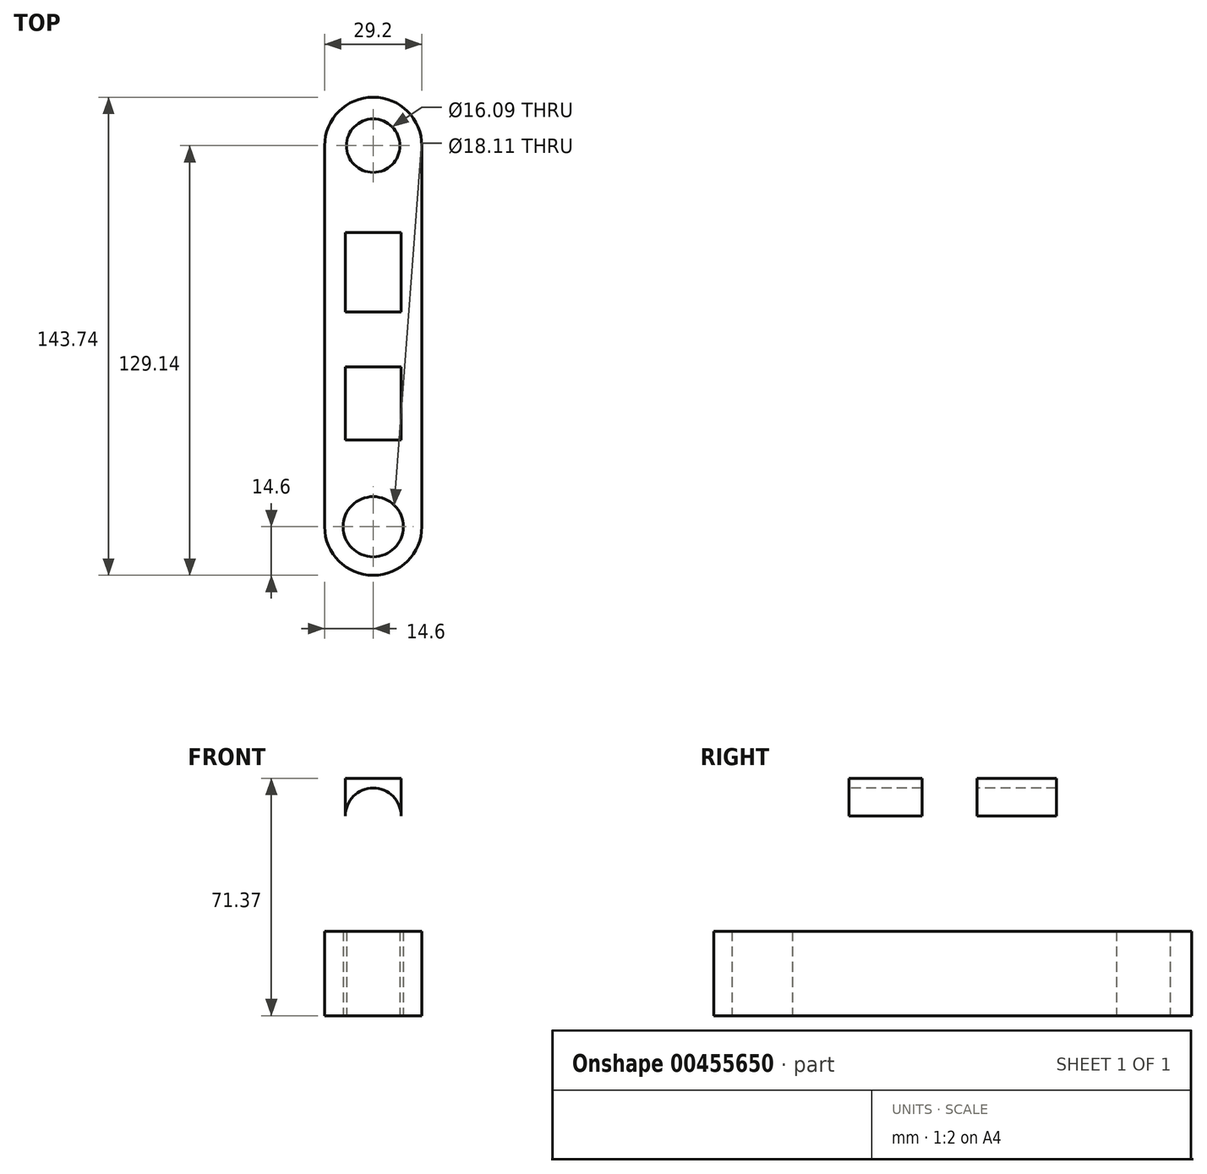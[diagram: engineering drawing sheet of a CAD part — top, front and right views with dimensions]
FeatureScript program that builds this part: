
annotation { "Feature Type Name" : "Feature", "Feature Type Description" : "" }
export const myFeature = defineFeature(function(context is Context, id is Id, definition is map)
    precondition{}
    {
        {
            var Q0;
            Q0=qCreatedBy(makeId("Top.planeOp"),FACE);
            var sketch = newSketch(context, id + "F0", { "sketchPlane" : qUnion([Q0])});
            skLineSegment(sketch, "E0.left", {"start": v(14.6, 57.27) * mm, "end": v(14.6, -57.27) * mm});
            skLineSegment(sketch, "E0.right", {"start": v(-14.6, 57.27) * mm, "end": v(-14.6, -57.27) * mm});
            skPoint(sketch, "E0.middle", {"position": v(0, 0) * mm});
            skArc(sketch, "E1", {"start": v(14.6, 57.27) * mm, "mid": v(0, 71.87) * mm, "end": v(-14.6, 57.27) * mm});
            skArc(sketch, "E2", {"start": v(14.6, -57.27) * mm, "mid": v(0, -71.87) * mm, "end": v(-14.6, -57.27) * mm});
            skCircle(sketch, "E3", {"center": v(0, 57.27) * mm, "radius": 8.04 * mm});
            skCircle(sketch, "E4", {"center": v(0, -57.27) * mm, "radius": 9.05 * mm});
            skSolve(sketch);
        }
        {
            var Q0;
            Q0=makeQuery(id+"F0.imprint","IMPRINT",FACE,{"disambiguationData":[TD([[makeQuery(id+"F0.imprint","IMPRINT",EDGE,{"derivedFrom":sQuery(id+"F0.wireOp",EDGE,"E0.left")}),-1.0]])]});
            extrude(context, id + "F1", {"entities" : qUnion([Q0]), "depth" : 25.4 * mm});
        }
        {
            var Q0;
            Q0=makeQuery(id+"F1.opExtrude","CAP_FACE",FACE,{"disambiguationData":[OSD([sQuery(id+"F0.wireOp",EDGE,"E0.left"),sQuery(id+"F0.wireOp",EDGE,"E0.right"),sQuery(id+"F0.wireOp",EDGE,"E1"),sQuery(id+"F0.wireOp",EDGE,"E2"),sQuery(id+"F0.wireOp",EDGE,"E3"),sQuery(id+"F0.wireOp",EDGE,"E4")])],"isStart":false});
            var sketch = newSketch(context, id + "F2", { "sketchPlane" : qUnion([Q0])});
            skLineSegment(sketch, "E5.bottom", {"start": v(8.42, 31.16) * mm, "end": v(-8.42, 31.16) * mm});
            skLineSegment(sketch, "E5.top", {"start": v(8.42, -31.16) * mm, "end": v(-8.42, -31.16) * mm});
            skLineSegment(sketch, "E5.left", {"start": v(8.42, 31.16) * mm, "end": v(8.42, -31.16) * mm});
            skLineSegment(sketch, "E5.right", {"start": v(-8.42, 31.16) * mm, "end": v(-8.42, -31.16) * mm});
            skPoint(sketch, "E5.middle", {"position": v(0, 0) * mm});
            skSolve(sketch);
        }
        {
            var Q0;
            Q0=makeQuery(id+"F2.imprint","IMPRINT",FACE,{"disambiguationData":[TD([[makeQuery(id+"F2.imprint","IMPRINT",EDGE,{"derivedFrom":sQuery(id+"F2.wireOp",EDGE,"E5.bottom")}),1.0]])]});
            extrude(context, id + "F3", {"entities" : qUnion([Q0]), "operationType" : NewBodyOperationType.ADD, "depth" : 45.97 * mm});
        }
        {
            var Q0;
            Q0=makeQuery(id+"F3.opExtrude","SWEPT_FACE",FACE,{"disambiguationData":[OSD([sQuery(id+"F2.wireOp",EDGE,"E5.left")])]});
            var sketch = newSketch(context, id + "F4", { "sketchPlane" : qUnion([Q0])});
            skLineSegment(sketch, "E6", {"start": v(-9.2, 71.37) * mm, "end": v(-9.2, 38.93) * mm});
            skLineSegment(sketch, "E7", {"start": v(7.32, 71.37) * mm, "end": v(7.32, 38.76) * mm});
            skArc(sketch, "E8", {"start": v(-9.2, 38.93) * mm, "mid": v(-1.02, 30.58) * mm, "end": v(7.32, 38.76) * mm});
            skSolve(sketch);
        }
        {
            var Q0;
            {var subQ0=sQuery(id+"F4.wireOp",EDGE,"E6");Q0=makeQuery(id+"F4.imprint","IMPRINT",FACE,{"disambiguationData":[TD([[makeQuery(id+"F4.imprint","IMPRINT",EDGE,{"derivedFrom":subQ0}),1.0]])]});}
            extrude(context, id + "F5", {"entities" : qUnion([Q0]), "operationType" : NewBodyOperationType.REMOVE, "oppositeDirection" : true, "depth" : 25.4 * mm});
        }
        {
            var Q0;
            Q0=makeQuery(id+"F3.opExtrude","SWEPT_FACE",FACE,{"disambiguationData":[OSD([sQuery(id+"F2.wireOp",EDGE,"E5.top")])]});
            var sketch = newSketch(context, id + "F6", { "sketchPlane" : qUnion([Q0])});
            skArc(sketch, "E9", {"start": v(-8.42, 59.98) * mm, "mid": v(0, 68.4) * mm, "end": v(8.42, 59.98) * mm});
            skCircle(sketch, "E10", {"center": v(0, 59.98) * mm, "radius": 4.36 * mm});
            skSolve(sketch);
        }
        {
            var Q0;
            {var subQ0=sQuery(id+"F6.wireOp",EDGE,"E9");Q0=makeQuery(id+"F6.imprint","IMPRINT",FACE,{"disambiguationData":[TD([[makeQuery(id+"F6.imprint","IMPRINT",EDGE,{"derivedFrom":subQ0}),1.0]])]});}
            var Q1;
            Q1=makeQuery(id+"F6.imprint","IMPRINT",FACE,{"disambiguationData":[TD([[makeQuery(id+"F6.imprint","IMPRINT",EDGE,{"derivedFrom":sQuery(id+"F6.wireOp",EDGE,"E10")}),1.0]])]});
            extrude(context, id + "F7", {"entities" : qUnion([Q0, Q1]), "operationType" : NewBodyOperationType.REMOVE, "oppositeDirection" : true, "depth" : 85.6 * mm});
        }
    });
